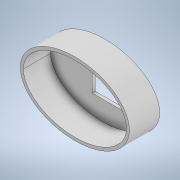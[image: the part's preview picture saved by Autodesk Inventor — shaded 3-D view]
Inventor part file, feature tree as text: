
AUTODESK INVENTOR PART (.ipt)
format: ipt  version: 2020 (Build 240168000, 168)  size: 129,536 bytes
history: native  units: mm
features: extrude x2, sketch x2, shell x1
ambient origin geometry x8: Origin, YZ Plane, XZ Plane, XY Plane, X Axis, Y Axis, Z Axis, Center Point
bodies: Solid1 (feature_tree)
feature tree (5):
  extrude  "Extrusion1"  Depth=50.0mm
  shell  "Shell1"  Thickness=50.0mm
  extrude  "Extrusion2"  Depth=50.0mm
  sketch  "Sketch1"  dims[d2=60.0mm d3=90.0mm d4=50.0mm d5=0.0mm]
  sketch  "Sketch2"  dims[d6=5.0mm d7=50.0mm d8=50.0mm d9=10.0mm d10=0.0mm]
